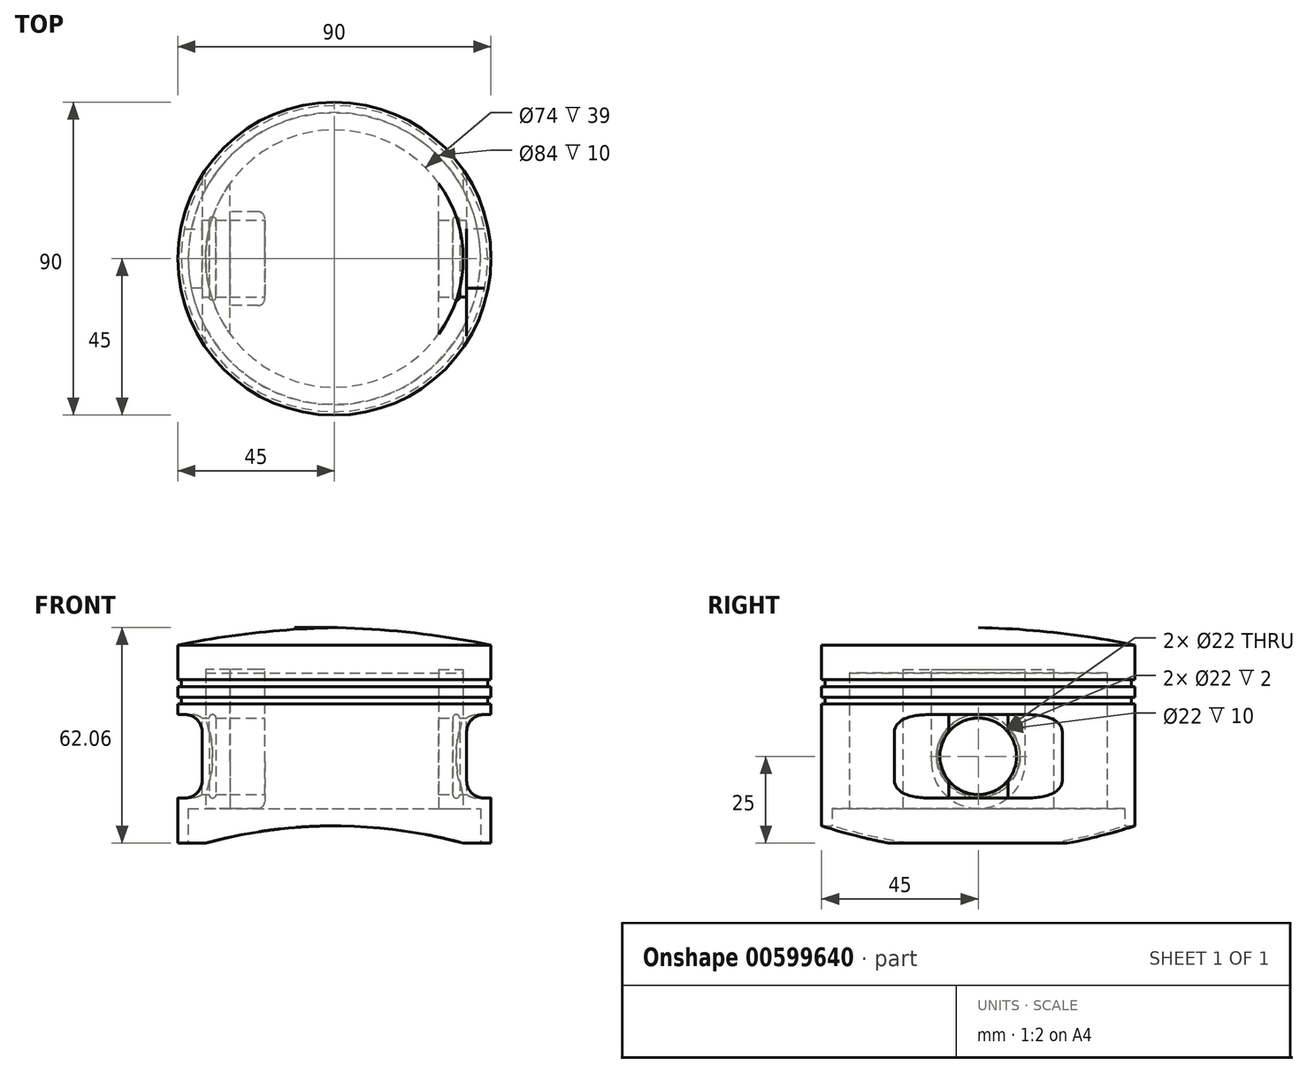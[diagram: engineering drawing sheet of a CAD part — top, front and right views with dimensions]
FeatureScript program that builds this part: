
annotation { "Feature Type Name" : "Feature", "Feature Type Description" : "" }
export const myFeature = defineFeature(function(context is Context, id is Id, definition is map)
    precondition{}
    {
        {
            var Q0;
            Q0=qCreatedBy(makeId("Front.planeOp"),FACE);
            var sketch = newSketch(context, id + "F0", { "sketchPlane" : qUnion([Q0])});
            skLineSegment(sketch, "E0.bottom", {"start": v(42, 0) * mm, "end": v(45, 0) * mm});
            skLineSegment(sketch, "E0.right", {"start": v(45, 0) * mm, "end": v(45, 40) * mm});
            skLineSegment(sketch, "E1", {"start": v(0, 49) * mm, "end": v(37, 49) * mm});
            skLineSegment(sketch, "E2", {"start": v(37, 49) * mm, "end": v(37, 10) * mm});
            skLineSegment(sketch, "E3", {"start": v(37, 10) * mm, "end": v(42, 10) * mm});
            skLineSegment(sketch, "E4", {"start": v(42, 10) * mm, "end": v(42, 0) * mm});
            skLineSegment(sketch, "E5", {"start": v(45, 40) * mm, "end": v(44, 40) * mm});
            skLineSegment(sketch, "E6", {"start": v(44, 40) * mm, "end": v(44, 42) * mm});
            skLineSegment(sketch, "E7", {"start": v(44, 42) * mm, "end": v(45, 42) * mm});
            skLineSegment(sketch, "E8.trimOffspring", {"start": v(45, 42) * mm, "end": v(45, 45) * mm});
            skLineSegment(sketch, "E9", {"start": v(45, 45) * mm, "end": v(44, 45) * mm});
            skLineSegment(sketch, "E10", {"start": v(44, 45) * mm, "end": v(44, 47) * mm});
            skLineSegment(sketch, "E11", {"start": v(44, 47) * mm, "end": v(45, 47) * mm});
            skLineSegment(sketch, "E12.trimOffspring", {"start": v(45, 47) * mm, "end": v(45, 57) * mm});
            skPoint(sketch, "E13", {"position": v(0, 62) * mm});
            skArc(sketch, "E14", {"start": v(45, 57) * mm, "mid": v(22.61, 60.5) * mm, "end": v(0, 62) * mm});
            skPoint(sketch, "E14.third.point", {"position": v(22.99, 60.45) * mm});
            skLineSegment(sketch, "E15", {"start": v(0, 49) * mm, "end": v(0, 62) * mm});
            skSolve(sketch);
        }
        {
            var Q0;
            Q0 = qSketchRegion(id + "F0", true);
            var Q1;
            Q1=sQuery(id+"F0.wireOp",EDGE,"E15");
            revolve(context, id + "F1", {"entities" : qUnion([Q0]), "axis" : qUnion([Q1]), "revolveType" : RevolveType.FULL});
        }
        {
            var Q0;
            Q0=qCreatedBy(makeId("Front.planeOp"),FACE);
            var sketch = newSketch(context, id + "F2", { "sketchPlane" : qUnion([Q0])});
            skPoint(sketch, "E16", {"position": v(45, 25) * mm});
            skLineSegment(sketch, "E17.bottom", {"start": v(38, 37) * mm, "end": v(52, 37) * mm});
            skLineSegment(sketch, "E17.top", {"start": v(38, 13) * mm, "end": v(52, 13) * mm});
            skLineSegment(sketch, "E17.left", {"start": v(38, 37) * mm, "end": v(38, 13) * mm});
            skLineSegment(sketch, "E17.right", {"start": v(52, 37) * mm, "end": v(52, 13) * mm});
            skLineSegment(sketch, "E18.MirrorCS", {"start": v(-38, 37) * mm, "end": v(-52, 37) * mm});
            skLineSegment(sketch, "E19.MirrorCS", {"start": v(-38, 37) * mm, "end": v(-38, 13) * mm});
            skLineSegment(sketch, "E20.MirrorCS", {"start": v(-38, 13) * mm, "end": v(-52, 13) * mm});
            skLineSegment(sketch, "E21.MirrorCS", {"start": v(-52, 37) * mm, "end": v(-52, 13) * mm});
            skSolve(sketch);
        }
        {
            var Q0;
            Q0 = qSketchRegion(id + "F2", true);
            extrude(context, id + "F3", {"entities" : qUnion([Q0]), "operationType" : NewBodyOperationType.REMOVE, "oppositeDirection" : true, "depth" : 40 * mm, "offsetDistance" : 25 * mm, "hasSecondDirection" : true, "secondDirectionOppositeDirection" : false, "secondDirectionDepth" : 40 * mm});
        }
        {
            var Q0;
            Q0=makeQuery(id+"F1.opRevolve","SWEPT_FACE",FACE,{"disambiguationData":[OSD([sQuery(id+"F0.wireOp",EDGE,"E3")])]});
            var sketch = newSketch(context, id + "F4", { "sketchPlane" : qUnion([Q0])});
            skLineSegment(sketch, "E22", {"start": v(30, 21.66) * mm, "end": v(30, -21.66) * mm});
            skLineSegment(sketch, "E23.MirrorCS", {"start": v(-30, 21.66) * mm, "end": v(-30, -21.66) * mm});
            skArc(sketch, "E24", {"start": v(-30, 21.66) * mm, "mid": v(-37, 0) * mm, "end": v(-30, -21.66) * mm});
            skArc(sketch, "E25", {"start": v(30, 21.66) * mm, "mid": v(37, 0) * mm, "end": v(30, -21.66) * mm});
            skSolve(sketch);
        }
        {
            var Q0;
            Q0 = qSketchRegion(id + "F4", true);
            extrude(context, id + "F5", {"entities" : qUnion([Q0]), "oppositeDirection" : true, "depth" : 40 * mm, "offsetDistance" : 25 * mm});
        }
        {
            var Q0;
            Q0=makeQuery(id+"F5.opExtrude","SWEPT_FACE",FACE,{"disambiguationData":[OSD([sQuery(id+"F4.wireOp",EDGE,"E23.MirrorCS")])]});
            var sketch = newSketch(context, id + "F6", { "sketchPlane" : qUnion([Q0])});
            skPoint(sketch, "E26", {"position": v(-21.66, 30) * mm});
            skPoint(sketch, "E27.endSnap0", {"position": v(0, 50) * mm});
            skLineSegment(sketch, "E28.0", {"start": v(-24.1, 37) * mm, "end": v(24.1, 37) * mm, "construction": true});
            skPoint(sketch, "E29.second.point", {"position": v(0, 37) * mm});
            skPoint(sketch, "E30", {"position": v(0, 10) * mm});
            skPoint(sketch, "E31", {"position": v(0, 23.5) * mm});
            skArc(sketch, "E32", {"start": v(-13.5, 23.5) * mm, "mid": v(0, 10) * mm, "end": v(13.5, 23.5) * mm});
            skLineSegment(sketch, "E33", {"start": v(-13.5, 23.5) * mm, "end": v(-13.5, 50) * mm});
            skLineSegment(sketch, "E34", {"start": v(13.5, 23.5) * mm, "end": v(13.5, 50) * mm});
            skLineSegment(sketch, "E35", {"start": v(-13.5, 50) * mm, "end": v(13.5, 50) * mm});
            skSolve(sketch);
        }
        {
            var Q0;
            Q0 = qSketchRegion(id + "F6", true);
            extrude(context, id + "F7", {"entities" : qUnion([Q0]), "depth" : 10 * mm, "offsetDistance" : 25 * mm});
        }
        {
            var Q0;
            Q0=makeQuery(id+"F3.boolean.opBoolean","COPY",FACE,{"derivedFrom":makeQuery(id+"F3.opExtrude","SWEPT_FACE",FACE,{"disambiguationData":[OSD([sQuery(id+"F2.wireOp",EDGE,"E17.left")])]})});
            var sketch = newSketch(context, id + "F8", { "sketchPlane" : qUnion([Q0])});
            skLineSegment(sketch, "E36", {"start": v(0, 37) * mm, "end": v(0, 13) * mm, "construction": true});
            skCircle(sketch, "E37", {"center": v(0, 25) * mm, "radius": 11 * mm});
            skSolve(sketch);
        }
        {
            var Q0;
            Q0 = qSketchRegion(id + "F8", true);
            extrude(context, id + "F9", {"entities" : qUnion([Q0]), "operationType" : NewBodyOperationType.REMOVE, "endBound" : BoundingType.THROUGH_ALL, "oppositeDirection" : true, "depth" : 25 * mm, "offsetDistance" : 25 * mm});
        }
        {
            var Q0;
            Q0=makeQuery(id+"F7.opExtrude","CAP_EDGE",EDGE,{"disambiguationData":[OSD([sQuery(id+"F6.wireOp",EDGE,"E33")])],"isStart":false});
            var Q1;
            Q1=makeQuery(id+"F7.opExtrude","CAP_EDGE",EDGE,{"disambiguationData":[OSD([sQuery(id+"F6.wireOp",EDGE,"E32")])],"isStart":false});
            var Q2;
            Q2=makeQuery(id+"Fo2aMk58Q4YXMpc_4.1.F7.opExtrude","CAP_EDGE",EDGE,{"disambiguationData":[OSD([sQuery(id+"F6.wireOp",EDGE,"E33")])],"isStart":false});
            fillet(context, id + "F10", {"entities" : qUnion([Q0, Q1, Q2]), "radius" : 2 * mm, "tangentPropagation" : true, "allowEdgeOverflow" : false});
        }
        {
            var Q0;
            Q0=makeQuery(id+"F3.boolean.opBoolean","COPY",EDGE,{"derivedFrom":makeQuery(id+"F3.opExtrude","SWEPT_EDGE",EDGE,{"disambiguationData":[OSD([sQuery(id+"F2.wireOp",EDGE,"E17.bottom"),sQuery(id+"F2.wireOp",EDGE,"E17.left")])]})});
            var Q1;
            Q1=makeQuery(id+"F3.boolean.opBoolean","COPY",EDGE,{"derivedFrom":makeQuery(id+"F3.opExtrude","SWEPT_EDGE",EDGE,{"disambiguationData":[OSD([sQuery(id+"F2.wireOp",EDGE,"E17.top"),sQuery(id+"F2.wireOp",EDGE,"E17.left")])]})});
            var Q2;
            Q2=makeQuery(id+"F3.boolean.opBoolean","COPY",EDGE,{"derivedFrom":makeQuery(id+"F3.opExtrude","SWEPT_EDGE",EDGE,{"disambiguationData":[OSD([sQuery(id+"F2.wireOp",EDGE,"E19.MirrorCS"),sQuery(id+"F2.wireOp",EDGE,"E20.MirrorCS")])]})});
            var Q3;
            Q3=makeQuery(id+"F3.boolean.opBoolean","COPY",EDGE,{"derivedFrom":makeQuery(id+"F3.opExtrude","SWEPT_EDGE",EDGE,{"disambiguationData":[OSD([sQuery(id+"F2.wireOp",EDGE,"E18.MirrorCS"),sQuery(id+"F2.wireOp",EDGE,"E19.MirrorCS")])]})});
            fillet(context, id + "F11", {"entities" : qUnion([Q0, Q1, Q2, Q3]), "radius" : 5 * mm, "tangentPropagation" : true, "allowEdgeOverflow" : false});
        }
        {
            var Q0;
            Q0=qCreatedBy(makeId("Front.planeOp"),FACE);
            var sketch = newSketch(context, id + "F12", { "sketchPlane" : qUnion([Q0])});
            skPoint(sketch, "E38", {"position": v(0, -135) * mm});
            skCircle(sketch, "E39", {"center": v(0, -135) * mm, "radius": 140 * mm});
            skSolve(sketch);
        }
        {
            var Q0;
            Q0 = qSketchRegion(id + "F12", true);
            extrude(context, id + "F13", {"entities" : qUnion([Q0]), "operationType" : NewBodyOperationType.REMOVE, "endBound" : BoundingType.SYMMETRIC, "depth" : 160 * mm, "offsetDistance" : 25 * mm});
        }
        {
            var Q0;
            Q0=qCreatedBy(makeId("Front.planeOp"),FACE);
            var sketch = newSketch(context, id + "F14", { "sketchPlane" : qUnion([Q0])});
            skLineSegment(sketch, "E40", {"start": v(0, 102.6) * mm, "end": v(0, -91.03) * mm, "construction": true});
            skLineSegment(sketch, "E41", {"start": v(-102.93, 0) * mm, "end": v(115.3, 0) * mm, "construction": true});
            skPoint(sketch, "E42", {"position": v(-35, 36) * mm});
            skCircle(sketch, "E43", {"center": v(-35, 36) * mm, "radius": 1 * mm});
            skCircle(sketch, "E44.MirrorC", {"center": v(35, 36) * mm, "radius": 1 * mm});
            skSolve(sketch);
        }
        {
            var Q0;
            Q0 = qSketchRegion(id + "F14", true);
            var Q1;
            {var subQ0=sQuery(id+"F6.wireOp",EDGE,"E35");var subQ1=sQuery(id+"F6.wireOp",EDGE,"E34");var subQ2=sQuery(id+"F6.wireOp",EDGE,"E33");var subQ3=sQuery(id+"F6.wireOp",EDGE,"E32");Q1=makeQuery(id+"F9.boolean.opBoolean","COPY",FACE,{"disambiguationData":[TD([makeQuery(id+"F7.opExtrude","CAP_FACE",FACE,{"disambiguationData":[OSD([subQ3,subQ2,subQ1,subQ0])],"isStart":true})])],"derivedFrom":makeQuery(id+"F9.opExtrude","SWEPT_FACE",FACE,{"disambiguationData":[OSD([sQuery(id+"F8.wireOp",EDGE,"E37")])]})});}
            revolve(context, id + "F15", {"operationType" : NewBodyOperationType.REMOVE, "entities" : qUnion([Q0]), "axis" : qUnion([Q1]), "revolveType" : RevolveType.FULL, "oppositeDirection" : true});
        }
    });
